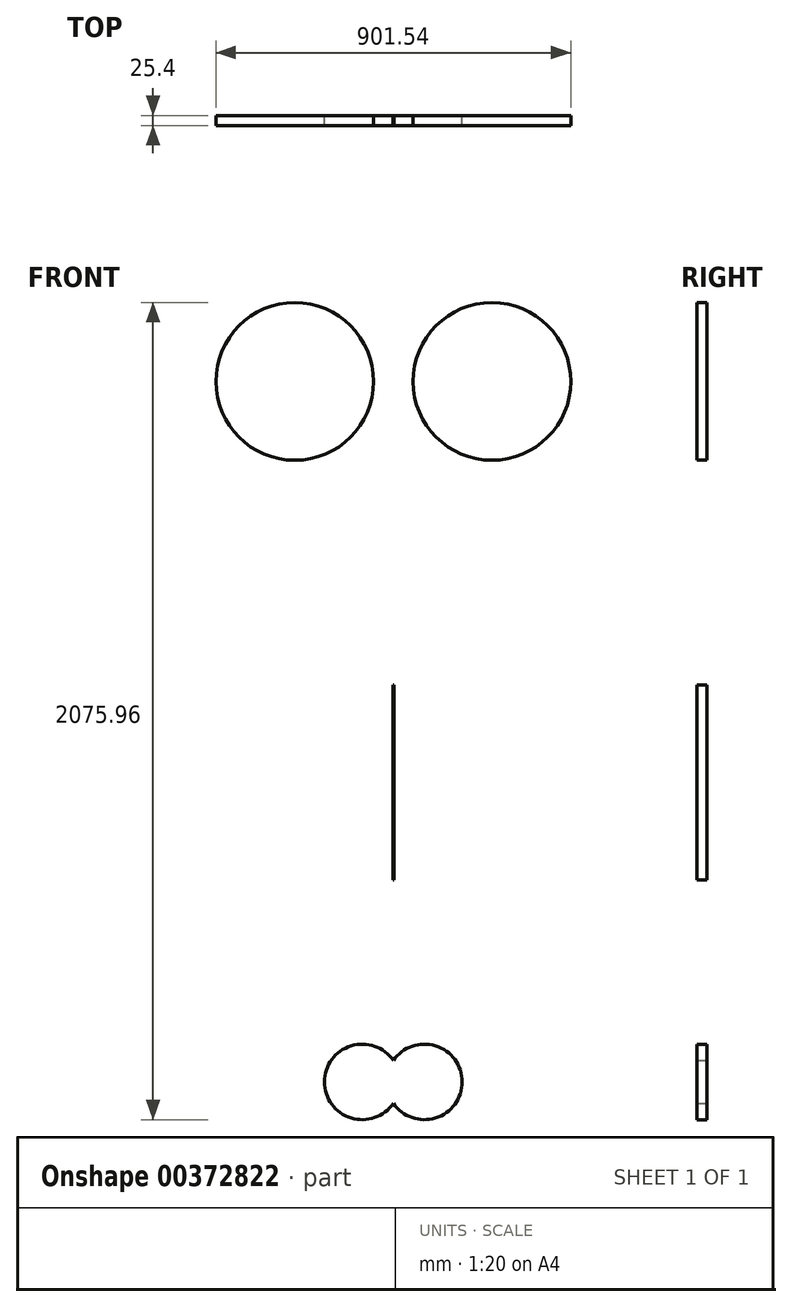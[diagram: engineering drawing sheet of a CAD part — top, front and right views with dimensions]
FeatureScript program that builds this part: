
annotation { "Feature Type Name" : "Feature", "Feature Type Description" : "" }
export const myFeature = defineFeature(function(context is Context, id is Id, definition is map)
    precondition{}
    {
        {
            var Q0;
            Q0=qCreatedBy(makeId("Front.planeOp"),FACE);
            var sketch = newSketch(context, id + "F0", { "sketchPlane" : qUnion([Q0])});
            skLineSegment(sketch, "E0.bottom", {"start": v(1.5, -308.35) * mm, "end": v(0, -308.35) * mm});
            skPoint(sketch, "E0.middle", {"position": v(0, -945.1) * mm});
            skPoint(sketch, "E0.top.end.orphan", {"position": v(-1.5, -1581.85) * mm});
            skPoint(sketch, "E0.top.start.orphan", {"position": v(105.15, -1581.85) * mm});
            skArc(sketch, "E1", {"start": v(-310.7, -1236.5) * mm, "mid": v(-316.6, -1232.7) * mm, "end": v(-322.77, -1229.34) * mm});
            skArc(sketch, "E2", {"start": v(-236.44, -1249.76) * mm, "mid": v(-245.68, -1259.53) * mm, "end": v(-253.38, -1270.54) * mm});
            skCircle(sketch, "E3", {"center": v(250.43, 462.46) * mm, "radius": 200.35 * mm});
            skArc(sketch, "E4.1.0", {"start": v(526, -747.87) * mm, "mid": v(435.76, -131.67) * mm, "end": v(-146.75, -351.97) * mm});
            skPoint(sketch, "E4.center", {"position": v(-239.35, -1278.88) * mm});
            skLineSegment(sketch, "E4.anchor1", {"start": v(-239.35, -1278.88) * mm, "end": v(-322.77, -1229.34) * mm, "construction": true});
            skLineSegment(sketch, "E4.anchor2", {"start": v(-239.35, -1278.88) * mm, "end": v(-236.44, -1249.76) * mm, "construction": true});
            skLineSegment(sketch, "E5", {"start": v(0, -945.1) * mm, "end": v(0, 1104.62) * mm});
            skPoint(sketch, "E6.orphan", {"position": v(-105.15, -308.35) * mm});
            skLineSegment(sketch, "E7", {"start": v(1.5, -308.35) * mm, "end": v(1.5, -944.34) * mm});
            skArc(sketch, "E8.trimOffspring", {"start": v(1.5, -944.34) * mm, "mid": v(61.4, -905.48) * mm, "end": v(56.05, -834.3) * mm});
            skCircle(sketch, "E9", {"center": v(-78.96, -1317.26) * mm, "radius": 95.88 * mm});
            skArc(sketch, "E10.trimOffspring", {"start": v(5.87, -804.76) * mm, "mid": v(2.94, -804.52) * mm, "end": v(0, -804.4) * mm});
            skArc(sketch, "E11.MirrorCS", {"start": v(236.44, -1249.76) * mm, "mid": v(245.68, -1259.53) * mm, "end": v(253.38, -1270.54) * mm});
            skLineSegment(sketch, "E12.MirrorCS", {"start": v(239.35, -1278.88) * mm, "end": v(236.44, -1249.76) * mm, "construction": true});
            skArc(sketch, "E13.MirrorCS", {"start": v(310.7, -1236.5) * mm, "mid": v(316.6, -1232.7) * mm, "end": v(322.77, -1229.34) * mm});
            skLineSegment(sketch, "E14.MirrorCS", {"start": v(-1.5, -308.35) * mm, "end": v(0, -308.35) * mm});
            skLineSegment(sketch, "E15.MirrorCS", {"start": v(239.35, -1278.88) * mm, "end": v(322.77, -1229.34) * mm, "construction": true});
            skArc(sketch, "E16.MirrorCS", {"start": v(-5.87, -804.76) * mm, "mid": v(-2.94, -804.52) * mm, "end": v(0, -804.4) * mm});
            skPoint(sketch, "E17.MirrorP", {"position": v(239.35, -1278.88) * mm});
            skPoint(sketch, "E18.MirrorP", {"position": v(105.15, -308.35) * mm});
            skCircle(sketch, "E19.MirrorC", {"center": v(78.96, -1317.26) * mm, "radius": 95.88 * mm});
            skArc(sketch, "E20.MirrorCS", {"start": v(-1.5, -944.34) * mm, "mid": v(-61.4, -905.48) * mm, "end": v(-56.05, -834.3) * mm});
            skLineSegment(sketch, "E21.MirrorCS", {"start": v(-1.5, -308.35) * mm, "end": v(-1.5, -944.34) * mm});
            skArc(sketch, "E22.MirrorCS", {"start": v(-526, -747.87) * mm, "mid": v(-435.76, -131.67) * mm, "end": v(146.75, -351.97) * mm});
            skCircle(sketch, "E23.MirrorC", {"center": v(-250.43, 462.46) * mm, "radius": 200.35 * mm});
            skSolve(sketch);
        }
        {
            var Q0;
            Q0 = qSketchRegion(id + "F0", true);
            extrude(context, id + "F1", {"entities" : qUnion([Q0]), "depth" : 25.4 * mm});
        }
    });
